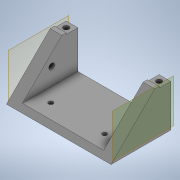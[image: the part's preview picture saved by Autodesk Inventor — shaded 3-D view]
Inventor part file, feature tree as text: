
AUTODESK INVENTOR PART (.ipt)
format: ipt  version: 2020 (Build 240168000, 168)  size: 602,624 bytes
history: native  units: mm
features: extrude x22, sketch x22, projected_geometry x9, chamfer x6, plane x5, mirror x2
ambient origin geometry x8: Origin, YZ Plane, XZ Plane, XY Plane, X Axis, Y Axis, Z Axis, Center Point
bodies: Solid1 (feature_tree)
feature tree (66):
  extrude  "Extrusion1"  Depth=120.0mm
  extrude  "Extrusion2"  TaperAngle=0.0deg  [1 undecoded]
  plane  "Work Plane2"
  extrude  "Extrusion6"  Depth=10.0mm
  plane  "Work Plane4"
  plane  "Work Plane5"
  extrude  "Extrusion7"  TaperAngle=0.0deg  [1 undecoded]
  extrude  "Extrusion8"  Depth=83.204mm TaperAngle=0.0deg
  chamfer  "Chamfer1"  Distance=20.747mm
  chamfer  "Chamfer2"  Distance=27.254mm
  chamfer  "Chamfer3"  Distance=2.0mm Angle=45.0deg
  chamfer  "Chamfer4"  Distance=6.0mm Angle=45.0deg
  chamfer  "Chamfer6"  [1 undecoded]
  extrude  "Extrusion9"  TaperAngle=0.0deg  [1 undecoded]
  extrude  "Extrusion10"  Depth=6.5mm
  extrude  "Extrusion11"  Depth=15.0mm
  extrude  "Extrusion12"  Depth=8.0mm
  mirror  "Mirror2"
  extrude  "WeaponMountSlot"  Depth=8.0mm TaperAngle=0.0deg
  chamfer  "Chamfer7"  Distance=10.0mm
  extrude  "Extrusion14"  Depth=8.0mm
  extrude  "Extrusion15"  Depth=55.8mm
  extrude  "Extrusion16"  Depth=2.0mm TaperAngle=45.0deg
  extrude  "Extrusion17"  Depth=8.0mm
  extrude  "WeaponMountHoles"  Depth=26.0mm
  extrude  "Extrusion19"  TaperAngle=0.0deg  [1 undecoded]
  extrude  "Extrusion20"  Depth=8.0mm
  extrude  "Extrusion21"  Depth=8.0mm
  mirror  "Mirror3"
  extrude  "Extrusion22"  Depth=8.0mm
  plane  "Work Plane7"
  extrude  "Extrusion23"  Depth=8.0mm
  plane  "Work Plane8"
  extrude  "Extrusion24"  Depth=7.0mm
  extrude  "Extrusion25"  TaperAngle=0.0deg  [1 undecoded]
  sketch  "Sketch1"  dims[d0=180.0mm d1=120.0mm]
  sketch  "Sketch3"  dims[d2=30.0mm d3=0.0mm]
  sketch  "Sketch7"  dims[d4=100.8mm d5=10.0mm]
  projected_geometry  "Projected Loop3"
  sketch  "Sketch9"  dims[d6=10.0mm d7=0.0mm d8=0.0mm]
  sketch  "Sketch10"  dims[d10=45.0deg d18=83.204mm d19=0.0mm d20=20.747mm d21=0.0mm d22=27.254mm d23=0.0mm]
  sketch  "Sketch11"  dims[d24=10.0mm d25=2.0mm d26=45.0deg]
  projected_geometry  "Projected Loop4"
  sketch  "Sketch12"  dims[d27=3.0mm d28=6.0mm d29=45.0deg]
  projected_geometry  "Projected Loop8"
  sketch  "Sketch16"  dims[d30=24.0mm]
  sketch  "Sketch17"  dims[d31=3.0mm]
  sketch  "Sketch18"  dims[d32=45.0deg]
  sketch  "Sketch19"  dims[d33=3.0mm]
  sketch  "Sketch20"  dims[d34=6.0mm]
  projected_geometry  "Projected Loop9"
  projected_geometry  "Projected Loop10"
  projected_geometry  "Projected Loop11"
  projected_geometry  "Projected Loop12"
  sketch  "Sketch21"  dims[d35=45.0deg]
  sketch  "Sketch22"  dims[d39=24.0mm]
  sketch  "Sketch23"  dims[d40=3.0mm]
  sketch  "Sketch24"  dims[d41=45.0deg]
  sketch  "Sketch25"  dims[d45=17.7mm]
  sketch  "Sketch26"  dims[d46=44.25mm d47=0.0mm d48=0.0mm]
  projected_geometry  "Projected Loop13"
  sketch  "Sketch27"  dims[d52=27.0mm d53=0.0mm]
  projected_geometry  "Projected Loop14"
  sketch  "Sketch30"  dims[d58=6.0mm d64=6.5mm]
  sketch  "Sketch31"  dims[d65=16.25mm d66=15.0mm]
  sketch  "Sketch32"  dims[d67=157.438mm d68=0.0mm d69=4.5mm d70=173.156mm d71=0.0mm d72=10.0mm d73=0.0mm d75=37.4mm d76=55.8mm d77=5.0mm d78=2.0mm d79=45.0deg d80=8.0mm d81=26.0mm d82=0.0mm d83=3.75mm d84=3.75mm d85=3.75mm d86=3.75mm d87=7.0mm d88=0.0mm d90=6.0mm d91=4.0mm d92=15.0mm d93=23.0mm d94=7.0mm d95=0.0mm d96=4.0mm d97=15.0mm d98=23.0mm d99=7.0mm d100=0.0mm d101=3.0mm d102=60.0mm d103=3.1mm d104=3.1mm d105=3.1mm d106=3.1mm d107=10.0mm d108=9.4mm d109=9.4mm d110=64.0mm d111=64.0mm d112=9.4mm d113=9.4mm d114=10.0mm d115=27.0mm d116=0.0mm d117=6.1mm d118=0.0mm d119=-7.853982mm d120=16.5mm d121=16.25mm d122=15.0mm d123=2.0mm d124=20.5mm d125=17.0mm d126=0.0mm d127=15.5mm d128=12.2mm d129=19.0mm d130=0.0mm d131=45.0deg d133=19.0mm d134=0.0mm d135=8.0mm d137=6.1mm d138=-8.0mm d139=0.0mm d140=0.0mm d141=-8.0mm d142=0.0mm d143=0.0mm d144=75.469mm d145=0.0mm]
note: 6 required parameter values undecoded (feature->parameter linkage not recoverable at this tier; creation-order binding heuristic only, values carry confidence <= 0.55)
